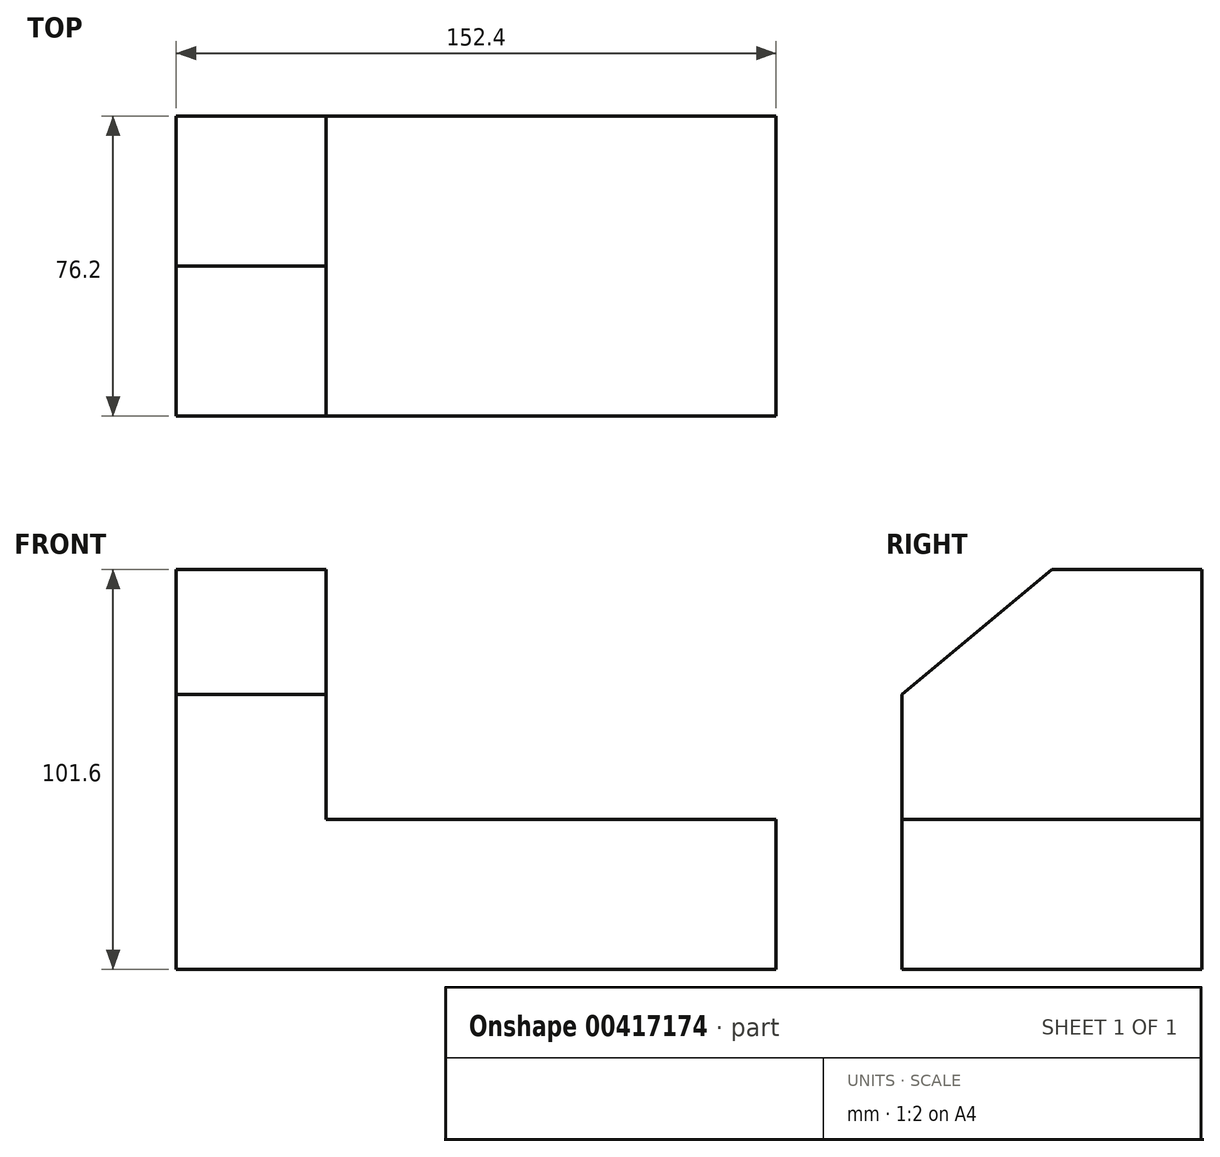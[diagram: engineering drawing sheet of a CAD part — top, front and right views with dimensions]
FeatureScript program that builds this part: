
annotation { "Feature Type Name" : "Feature", "Feature Type Description" : "" }
export const myFeature = defineFeature(function(context is Context, id is Id, definition is map)
    precondition{}
    {
        {
            var Q0;
            Q0=qCreatedBy(makeId("Front.planeOp"),FACE);
            var sketch = newSketch(context, id + "F0", { "sketchPlane" : qUnion([Q0])});
            skLineSegment(sketch, "E0", {"start": v(0, 0) * mm, "end": v(152.4, 0) * mm});
            skLineSegment(sketch, "E1", {"start": v(152.4, 0) * mm, "end": v(152.4, 38.1) * mm});
            skLineSegment(sketch, "E2", {"start": v(152.4, 38.1) * mm, "end": v(38.1, 38.1) * mm});
            skLineSegment(sketch, "E3", {"start": v(38.1, 38.1) * mm, "end": v(38.1, 101.6) * mm});
            skLineSegment(sketch, "E4", {"start": v(38.1, 101.6) * mm, "end": v(0, 101.6) * mm});
            skLineSegment(sketch, "E5", {"start": v(0, 101.6) * mm, "end": v(0, 0) * mm});
            skSolve(sketch);
        }
        {
            var Q0;
            Q0=makeQuery(id+"F0.imprint","IMPRINT",FACE,{"disambiguationData":[TD([[makeQuery(id+"F0.imprint","IMPRINT",EDGE,{"derivedFrom":sQuery(id+"F0.wireOp",EDGE,"E0")}),1.0]])]});
            extrude(context, id + "F1", {"entities" : qUnion([Q0]), "depth" : 76.2 * mm});
        }
        {
            var Q0;
            Q0=makeQuery(id+"F1.opExtrude","SWEPT_FACE",FACE,{"disambiguationData":[OSD([sQuery(id+"F0.wireOp",EDGE,"E3")])]});
            var sketch = newSketch(context, id + "F2", { "sketchPlane" : qUnion([Q0])});
            skLineSegment(sketch, "E6", {"start": v(-38.1, 101.6) * mm, "end": v(-76.2, 69.85) * mm});
            skLineSegment(sketch, "E7", {"start": v(-109.33, 89.48) * mm, "end": v(-108.08, 87.8) * mm});
            skSolve(sketch);
        }
        {
            var Q0;
            Q0 = qSketchRegion(id + "F2", true);
            var Q1;
            {var subQ0=sQuery(id+"F2.wireOp",EDGE,"E6");Q1=makeQuery(id+"F2.imprint","IMPRINT",FACE,{"disambiguationData":[TD([[makeQuery(id+"F2.imprint","IMPRINT",EDGE,{"derivedFrom":subQ0}),-1.0]])]});}
            extrude(context, id + "F3", {"entities" : qUnion([Q0, Q1]), "operationType" : NewBodyOperationType.REMOVE, "endBound" : BoundingType.THROUGH_ALL, "oppositeDirection" : true, "depth" : 25.4 * mm});
        }
    });
